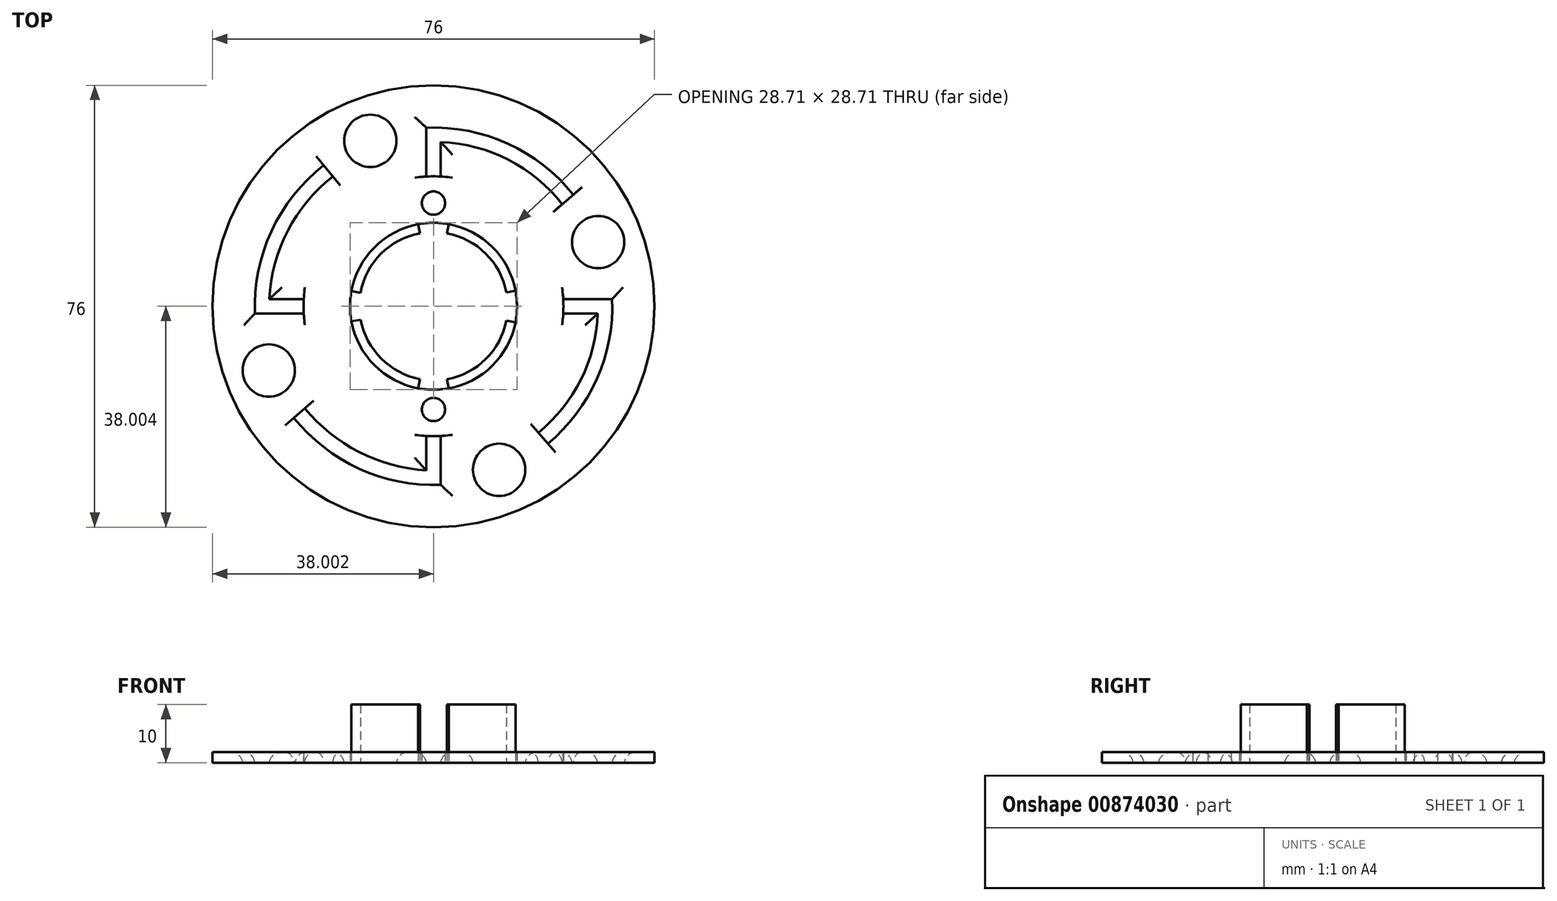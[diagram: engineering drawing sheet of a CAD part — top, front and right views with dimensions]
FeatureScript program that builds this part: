
annotation { "Feature Type Name" : "Feature", "Feature Type Description" : "" }
export const myFeature = defineFeature(function(context is Context, id is Id, definition is map)
    precondition{}
    {
        {
            var Q0;
            Q0=qCreatedBy(makeId("Top.planeOp"),FACE);
            var sketch = newSketch(context, id + "F0", { "sketchPlane" : qUnion([Q0])});
            skCircle(sketch, "E0", {"center": v(0, 0) * mm, "radius": 20.75 * mm});
            skCircle(sketch, "E1", {"center": v(0, 0) * mm, "radius": 22.35 * mm});
            skArc(sketch, "E2", {"start": v(-17.32, 22.32) * mm, "mid": v(-25.07, 12.97) * mm, "end": v(-28.22, 1.25) * mm});
            skLineSegment(sketch, "E3", {"start": v(-30.72, -1.25) * mm, "end": v(-20.71, -1.25) * mm});
            skLineSegment(sketch, "E4", {"start": v(-28.22, 1.25) * mm, "end": v(-20.71, 1.25) * mm});
            skArc(sketch, "E5", {"start": v(18.04, -21.74) * mm, "mid": v(25.36, -12.6) * mm, "end": v(28.22, -1.25) * mm});
            skLineSegment(sketch, "E6", {"start": v(30.72, 1.25) * mm, "end": v(20.71, 1.25) * mm});
            skLineSegment(sketch, "E7", {"start": v(28.22, -1.25) * mm, "end": v(20.71, -1.25) * mm});
            skArc(sketch, "E8", {"start": v(-22.14, -17.55) * mm, "mid": v(-12.8, -25.06) * mm, "end": v(-1.25, -28.22) * mm});
            skArc(sketch, "E9", {"start": v(22.14, 17.55) * mm, "mid": v(12.88, 25.2) * mm, "end": v(1.25, 28.22) * mm});
            skLineSegment(sketch, "E10", {"start": v(-1.25, -28.22) * mm, "end": v(-1.25, -20.71) * mm});
            skLineSegment(sketch, "E11", {"start": v(1.25, -20.71) * mm, "end": v(1.25, -30.72) * mm});
            skLineSegment(sketch, "E12", {"start": v(1.25, 28.22) * mm, "end": v(1.25, 20.71) * mm});
            skLineSegment(sketch, "E13", {"start": v(-1.25, 30.72) * mm, "end": v(-1.25, 20.71) * mm});
            skLineSegment(sketch, "E14", {"start": v(0, 20.75) * mm, "end": v(0, 17.75) * mm});
            skLineSegment(sketch, "E15", {"start": v(0, -20.75) * mm, "end": v(0, -17.75) * mm});
            skArc(sketch, "E16", {"start": v(-14.12, 2.6) * mm, "mid": v(-14.35, 0) * mm, "end": v(-14.12, -2.6) * mm});
            skArc(sketch, "E17", {"start": v(-2.61, -14.12) * mm, "mid": v(0, -14.35) * mm, "end": v(2.62, -14.12) * mm});
            skArc(sketch, "E18", {"start": v(14.1, -2.75) * mm, "mid": v(14.36, -0.03) * mm, "end": v(14.1, 2.7) * mm});
            skArc(sketch, "E19", {"start": v(2.61, 14.12) * mm, "mid": v(0, 14.36) * mm, "end": v(-2.61, 14.12) * mm});
            skCircle(sketch, "E20", {"center": v(11.28, -28.12) * mm, "radius": 4.5 * mm});
            skCircle(sketch, "E21", {"center": v(28.32, 11.04) * mm, "radius": 4.5 * mm});
            skCircle(sketch, "E22", {"center": v(-10.86, 28.46) * mm, "radius": 4.5 * mm});
            skCircle(sketch, "E23", {"center": v(-28.32, -11.04) * mm, "radius": 4.5 * mm});
            skLineSegment(sketch, "E24", {"start": v(-2.61, 14.12) * mm, "end": v(-2.32, 12.55) * mm});
            skLineSegment(sketch, "E25", {"start": v(2.61, 14.12) * mm, "end": v(2.32, 12.55) * mm});
            skLineSegment(sketch, "E26", {"start": v(-14.12, 2.6) * mm, "end": v(-12.55, 2.3) * mm});
            skLineSegment(sketch, "E27", {"start": v(-14.12, -2.6) * mm, "end": v(-12.55, -2.3) * mm});
            skLineSegment(sketch, "E28", {"start": v(-2.61, -14.12) * mm, "end": v(-2.32, -12.55) * mm});
            skLineSegment(sketch, "E29", {"start": v(14.1, 2.7) * mm, "end": v(12.53, 2.4) * mm});
            skLineSegment(sketch, "E30", {"start": v(14.1, -2.75) * mm, "end": v(12.52, -2.45) * mm});
            skLineSegment(sketch, "E31", {"start": v(2.62, -14.12) * mm, "end": v(2.32, -12.55) * mm});
            skArc(sketch, "E32", {"start": v(-12.55, -2.3) * mm, "mid": v(-8.99, -8.98) * mm, "end": v(-2.32, -12.55) * mm});
            skArc(sketch, "E33", {"start": v(-14.12, -2.6) * mm, "mid": v(-10.14, -10.13) * mm, "end": v(-2.61, -14.12) * mm});
            skArc(sketch, "E34", {"start": v(2.62, -14.12) * mm, "mid": v(10.12, -10.22) * mm, "end": v(14.1, -2.75) * mm});
            skArc(sketch, "E35", {"start": v(2.32, -12.55) * mm, "mid": v(8.99, -9.08) * mm, "end": v(12.52, -2.45) * mm});
            skArc(sketch, "E36", {"start": v(14.1, 2.7) * mm, "mid": v(10.13, 10.2) * mm, "end": v(2.61, 14.12) * mm});
            skArc(sketch, "E37", {"start": v(12.53, 2.4) * mm, "mid": v(9, 9.06) * mm, "end": v(2.32, 12.55) * mm});
            skArc(sketch, "E38", {"start": v(-2.32, 12.55) * mm, "mid": v(-9.04, 9.03) * mm, "end": v(-12.55, 2.3) * mm});
            skArc(sketch, "E39", {"start": v(-2.61, 14.12) * mm, "mid": v(-10.15, 10.15) * mm, "end": v(-14.12, 2.6) * mm});
            skPoint(sketch, "E40", {"position": v(-24.02, -19.2) * mm});
            skPoint(sketch, "E41", {"position": v(-18.9, 24.26) * mm});
            skPoint(sketch, "E42", {"position": v(24.02, 19.2) * mm});
            skPoint(sketch, "E43", {"position": v(19.68, -23.63) * mm});
            skArc(sketch, "E44", {"start": v(-24.02, -19.2) * mm, "mid": v(-12.75, -27.96) * mm, "end": v(1.25, -30.72) * mm});
            skArc(sketch, "E45", {"start": v(19.68, -23.63) * mm, "mid": v(28.11, -12.48) * mm, "end": v(30.72, 1.25) * mm});
            skArc(sketch, "E46", {"start": v(24.02, 19.2) * mm, "mid": v(12.77, 27.98) * mm, "end": v(-1.25, 30.72) * mm});
            skArc(sketch, "E47", {"start": v(-18.9, 24.26) * mm, "mid": v(-27.87, 12.92) * mm, "end": v(-30.72, -1.25) * mm});
            skLineSegment(sketch, "E48", {"start": v(-18.9, 24.26) * mm, "end": v(-17.32, 22.32) * mm});
            skLineSegment(sketch, "E49", {"start": v(22.14, 17.55) * mm, "end": v(24.02, 19.2) * mm});
            skLineSegment(sketch, "E50", {"start": v(18.04, -21.74) * mm, "end": v(19.68, -23.63) * mm});
            skLineSegment(sketch, "E51", {"start": v(-24.02, -19.2) * mm, "end": v(-22.14, -17.55) * mm});
            skCircle(sketch, "E52", {"center": v(0, 0) * mm, "radius": 38 * mm});
            skSolve(sketch);
        }
        {
            var Q0;
            Q0=makeQuery(id+"F0.imprint","IMPRINT",FACE,{"disambiguationData":[TD([[makeQuery(id+"F0.imprint","IMPRINT",EDGE,{"derivedFrom":sQuery(id+"F0.wireOp",EDGE,"JtYkX3aF-uqA7-pjmF-8fSk-2beL0rNtP7QC")}),-1.0]])]});
            var Q1;
            Q1=makeQuery(id+"F0.imprint","IMPRINT",FACE,{"disambiguationData":[TD([[makeQuery(id+"F0.imprint","IMPRINT",EDGE,{"derivedFrom":sQuery(id+"F0.wireOp",EDGE,"8JJW8lRD-QEWP-9C01-VRjb-YcTUdrWMRwsa")}),1.0]])]});
            var Q2;
            {var subQ1=sQuery(id+"F0.wireOp",EDGE,"NE2U6Hh3-jpx8-j1Jv-iiVe-F0KoeOMKkSiu");Q2=makeQuery(id+"F0.imprint","IMPRINT",FACE,{"disambiguationData":[TD([[makeQuery(id+"F0.imprint","IMPRINT",EDGE,{"derivedFrom":subQ1}),-1.0]])]});}
            var Q3;
            {var subQ1=sQuery(id+"F0.wireOp",EDGE,"E5");Q3=makeQuery(id+"F0.imprint","IMPRINT",FACE,{"disambiguationData":[TD([[makeQuery(id+"F0.imprint","IMPRINT",EDGE,{"derivedFrom":subQ1}),1.0]])]});}
            var Q4;
            {var subQ0=sQuery(id+"F0.wireOp",EDGE,"E4");var subQ1=sQuery(id+"F0.wireOp",EDGE,"E0");var subQ2=makeQuery(id+"F0.imprint","INTERSECT",VERTEX,{"derivedFrom":[subQ1,subQ0]});Q4=makeQuery(id+"F0.imprint","IMPRINT",FACE,{"disambiguationData":[TD([[makeQuery(id+"F0.imprint","IMPRINT",EDGE,{"disambiguationData":[TD([[subQ2,1.0]])],"derivedFrom":subQ1}),-1.0]])]});}
            var Q5;
            {var subQ0=sQuery(id+"F0.wireOp",EDGE,"E3");var subQ1=sQuery(id+"F0.wireOp",EDGE,"E0");var subQ2=makeQuery(id+"F0.imprint","INTERSECT",VERTEX,{"derivedFrom":[subQ1,subQ0]});Q5=makeQuery(id+"F0.imprint","IMPRINT",FACE,{"disambiguationData":[TD([[makeQuery(id+"F0.imprint","IMPRINT",EDGE,{"disambiguationData":[TD([[subQ2,1.0]])],"derivedFrom":subQ1}),-1.0]])]});}
            var Q6;
            {var subQ0=sQuery(id+"F0.wireOp",EDGE,"E10");var subQ1=sQuery(id+"F0.wireOp",EDGE,"E0");var subQ2=makeQuery(id+"F0.imprint","INTERSECT",VERTEX,{"derivedFrom":[subQ1,subQ0]});Q6=makeQuery(id+"F0.imprint","IMPRINT",FACE,{"disambiguationData":[TD([[makeQuery(id+"F0.imprint","IMPRINT",EDGE,{"disambiguationData":[TD([[subQ2,-1.0]])],"derivedFrom":subQ1}),-1.0]])]});}
            var Q7;
            {var subQ0=sQuery(id+"F0.wireOp",EDGE,"E7");var subQ1=sQuery(id+"F0.wireOp",EDGE,"E0");var subQ2=makeQuery(id+"F0.imprint","INTERSECT",VERTEX,{"derivedFrom":[subQ1,subQ0]});Q7=makeQuery(id+"F0.imprint","IMPRINT",FACE,{"disambiguationData":[TD([[makeQuery(id+"F0.imprint","IMPRINT",EDGE,{"disambiguationData":[TD([[subQ2,1.0]])],"derivedFrom":subQ1}),-1.0]])]});}
            var Q8;
            {var subQ0=sQuery(id+"F0.wireOp",EDGE,"E6");var subQ1=sQuery(id+"F0.wireOp",EDGE,"E0");var subQ2=makeQuery(id+"F0.imprint","INTERSECT",VERTEX,{"derivedFrom":[subQ1,subQ0]});Q8=makeQuery(id+"F0.imprint","IMPRINT",FACE,{"disambiguationData":[TD([[makeQuery(id+"F0.imprint","IMPRINT",EDGE,{"disambiguationData":[TD([[subQ2,1.0]])],"derivedFrom":subQ1}),-1.0]])]});}
            var Q9;
            {var subQ0=sQuery(id+"F0.wireOp",EDGE,"E6");var subQ1=sQuery(id+"F0.wireOp",EDGE,"E0");var subQ2=makeQuery(id+"F0.imprint","INTERSECT",VERTEX,{"derivedFrom":[subQ1,subQ0]});Q9=makeQuery(id+"F0.imprint","IMPRINT",FACE,{"disambiguationData":[TD([[makeQuery(id+"F0.imprint","IMPRINT",EDGE,{"disambiguationData":[TD([[subQ2,-1.0]])],"derivedFrom":subQ1}),-1.0]])]});}
            var Q10;
            {var subQ0=sQuery(id+"F0.wireOp",EDGE,"E12");var subQ1=sQuery(id+"F0.wireOp",EDGE,"E0");var subQ2=makeQuery(id+"F0.imprint","INTERSECT",VERTEX,{"derivedFrom":[subQ1,subQ0]});Q10=makeQuery(id+"F0.imprint","IMPRINT",FACE,{"disambiguationData":[TD([[makeQuery(id+"F0.imprint","IMPRINT",EDGE,{"disambiguationData":[TD([[subQ2,-1.0]])],"derivedFrom":subQ1}),-1.0]])]});}
            var Q11;
            {var subQ0=sQuery(id+"F0.wireOp",EDGE,"E3");var subQ1=sQuery(id+"F0.wireOp",EDGE,"E0");var subQ2=makeQuery(id+"F0.imprint","INTERSECT",VERTEX,{"derivedFrom":[subQ1,subQ0]});Q11=makeQuery(id+"F0.imprint","IMPRINT",FACE,{"disambiguationData":[TD([[makeQuery(id+"F0.imprint","IMPRINT",EDGE,{"disambiguationData":[TD([[subQ2,-1.0]])],"derivedFrom":subQ1}),-1.0]])]});}
            var Q12;
            {var subQ0=sQuery(id+"F0.wireOp",EDGE,"E0");var subQ5=makeQuery(id+"F0.imprint","INTERSECT",VERTEX,{"derivedFrom":[subQ0,sQuery(id+"F0.wireOp",EDGE,"E6")]});Q12=makeQuery(id+"F0.imprint","IMPRINT",FACE,{"disambiguationData":[TD([[makeQuery(id+"F0.imprint","IMPRINT",EDGE,{"disambiguationData":[TD([[subQ5,-1.0]])],"derivedFrom":subQ0}),1.0]])]});}
            var Q13;
            Q13=makeQuery(id+"F0.imprint","IMPRINT",FACE,{"disambiguationData":[TD([[makeQuery(id+"F0.imprint","IMPRINT",EDGE,{"derivedFrom":sQuery(id+"F0.wireOp",EDGE,"3ZusnNTy-GkZT-iUSi-foyf-aXQAiV7al5yb")}),-1.0]])]});
            extrude(context, id + "F1", {"entities" : qUnion([Q0, Q1, Q2, Q3, Q4, Q5, Q6, Q7, Q8, Q9, Q10, Q11, Q12, Q13]), "depth" : 1.8 * mm, "offsetDistance" : 25 * mm});
        }
        {
            var Q0;
            Q0=sQuery(id+"F0.wireOp",VERTEX,"E15.end");
            var Q1;
            Q1=sQuery(id+"F0.wireOp",VERTEX,"E14.end");
            var Q2;
            Q2=makeQuery(id+"F1.opExtrude","SWEPT_BODY",BODY,{"disambiguationData":[OSD([sQuery(id+"F0.wireOp",EDGE,"E1"),sQuery(id+"F0.wireOp",EDGE,"JtYkX3aF-uqA7-pjmF-8fSk-2beL0rNtP7QC"),sQuery(id+"F0.wireOp",EDGE,"8JJW8lRD-QEWP-9C01-VRjb-YcTUdrWMRwsa"),sQuery(id+"F0.wireOp",EDGE,"uFhvHYX3-8JKD-H8n8-qWPz-aUgkWJzXKccN"),sQuery(id+"F0.wireOp",EDGE,"E2"),sQuery(id+"F0.wireOp",EDGE,"E3"),sQuery(id+"F0.wireOp",EDGE,"E4"),sQuery(id+"F0.wireOp",EDGE,"E5"),sQuery(id+"F0.wireOp",EDGE,"NE2U6Hh3-jpx8-j1Jv-iiVe-F0KoeOMKkSiu"),sQuery(id+"F0.wireOp",EDGE,"E6"),sQuery(id+"F0.wireOp",EDGE,"E7"),sQuery(id+"F0.wireOp",EDGE,"ZG8jGtW0-kf8V-TbsZ-LPp7-RuGRRNqqyVkH"),sQuery(id+"F0.wireOp",EDGE,"fmeD1r8i-8Wsa-lR9i-GNXP-AYA1yHY84zb3"),sQuery(id+"F0.wireOp",EDGE,"bjy13ZNf-o2fh-lKbF-fSuF-RSpPyinbBZMj"),sQuery(id+"F0.wireOp",EDGE,"E8"),sQuery(id+"F0.wireOp",EDGE,"YXEZxhNc-pCvv-fJSu-8syy-bRr3xrhN3yT2"),sQuery(id+"F0.wireOp",EDGE,"nJSUC5IB-OxOl-JQJy-F9vk-B84e3hYhLg1p"),sQuery(id+"F0.wireOp",EDGE,"E9"),sQuery(id+"F0.wireOp",EDGE,"A251WNtt-zrTg-3Hvl-hV5r-WAsRRatjA8sI"),sQuery(id+"F0.wireOp",EDGE,"ZfxGHPmq-kaDy-ZfHD-nUsA-2Ftj0pm5jEMy"),sQuery(id+"F0.wireOp",EDGE,"E10"),sQuery(id+"F0.wireOp",EDGE,"E11"),sQuery(id+"F0.wireOp",EDGE,"E12"),sQuery(id+"F0.wireOp",EDGE,"E13"),sQuery(id+"F0.wireOp",EDGE,"weULgePI-roOJ-cMUK-peC7-qsmyXOXqrT9m"),sQuery(id+"F0.wireOp",EDGE,"UDUuayih-Ka7P-NoIc-IkLO-qXrikWTbf6pt"),sQuery(id+"F0.wireOp",EDGE,"T07nDOxv-luDJ-uSm4-Lqdw-o2tEsc6Tqr3Y"),sQuery(id+"F0.wireOp",EDGE,"01p4Yr1x-TUeZ-ZZvR-0jQk-AZIFxx44rd4s"),sQuery(id+"F0.wireOp",EDGE,"mddWgEqq-aVu1-2llw-zfOM-TSO3SZ2z48u3")])]});
            hole(context, id + "F2", {"style" : HoleStyle.SIMPLE, "endStyle" : HoleEndStyle.THROUGH, "oppositeDirection" : true, "holeDiameter" : 4 * mm, "majorDiameter" : 5 * mm, "isTappedThrough" : true, "tappedDepth" : 12 * mm, "tapClearance" : 3, "locations" : qUnion([Q0, Q1]), "scope" : qUnion([Q2])});
        }
        {
            var Q0;
            Q0=makeQuery(id+"F1.opExtrude","CAP_EDGE",EDGE,{"disambiguationData":[OSD([sQuery(id+"F0.wireOp",EDGE,"mddWgEqq-aVu1-2llw-zfOM-TSO3SZ2z48u3")])],"isStart":false});
            var Q1;
            Q1=makeQuery(id+"F1.opExtrude","CAP_EDGE",EDGE,{"disambiguationData":[OSD([sQuery(id+"F0.wireOp",EDGE,"UDUuayih-Ka7P-NoIc-IkLO-qXrikWTbf6pt")])],"isStart":false});
            var Q2;
            Q2=makeQuery(id+"F1.opExtrude","CAP_EDGE",EDGE,{"disambiguationData":[OSD([sQuery(id+"F0.wireOp",EDGE,"01p4Yr1x-TUeZ-ZZvR-0jQk-AZIFxx44rd4s")])],"isStart":false});
            var Q3;
            Q3=makeQuery(id+"F1.opExtrude","CAP_EDGE",EDGE,{"disambiguationData":[OSD([sQuery(id+"F0.wireOp",EDGE,"T07nDOxv-luDJ-uSm4-Lqdw-o2tEsc6Tqr3Y")])],"isStart":false});
            var Q4;
            Q4=makeQuery(id+"F1.opExtrude","CAP_EDGE",EDGE,{"disambiguationData":[OSD([sQuery(id+"F0.wireOp",EDGE,"E5")])],"isStart":false});
            var Q5;
            Q5=makeQuery(id+"F1.opExtrude","CAP_EDGE",EDGE,{"disambiguationData":[OSD([sQuery(id+"F0.wireOp",EDGE,"E8")])],"isStart":false});
            var Q6;
            Q6=makeQuery(id+"F1.opExtrude","CAP_EDGE",EDGE,{"disambiguationData":[OSD([sQuery(id+"F0.wireOp",EDGE,"E2")])],"isStart":false});
            var Q7;
            Q7=makeQuery(id+"F1.opExtrude","CAP_EDGE",EDGE,{"disambiguationData":[OSD([sQuery(id+"F0.wireOp",EDGE,"E9")])],"isStart":false});
            var Q8;
            Q8=makeQuery(id+"F1.opExtrude","CAP_EDGE",EDGE,{"disambiguationData":[OSD([sQuery(id+"F0.wireOp",EDGE,"8JJW8lRD-QEWP-9C01-VRjb-YcTUdrWMRwsa")])],"isStart":false});
            var Q9;
            Q9=makeQuery(id+"F1.opExtrude","CAP_EDGE",EDGE,{"disambiguationData":[OSD([sQuery(id+"F0.wireOp",EDGE,"JtYkX3aF-uqA7-pjmF-8fSk-2beL0rNtP7QC")])],"isStart":false});
            var Q10;
            Q10=makeQuery(id+"F1.opExtrude","CAP_EDGE",EDGE,{"disambiguationData":[OSD([sQuery(id+"F0.wireOp",EDGE,"E4")])],"isStart":false});
            var Q11;
            Q11=makeQuery(id+"F1.opExtrude","CAP_EDGE",EDGE,{"disambiguationData":[OSD([sQuery(id+"F0.wireOp",EDGE,"E3")])],"isStart":false});
            var Q12;
            Q12=makeQuery(id+"F1.opExtrude","CAP_EDGE",EDGE,{"disambiguationData":[OSD([sQuery(id+"F0.wireOp",EDGE,"E13")])],"isStart":false});
            var Q13;
            Q13=makeQuery(id+"F1.opExtrude","CAP_EDGE",EDGE,{"disambiguationData":[OSD([sQuery(id+"F0.wireOp",EDGE,"E12")])],"isStart":false});
            var Q14;
            Q14=makeQuery(id+"F1.opExtrude","CAP_EDGE",EDGE,{"disambiguationData":[OSD([sQuery(id+"F0.wireOp",EDGE,"E6")])],"isStart":false});
            var Q15;
            Q15=makeQuery(id+"F1.opExtrude","CAP_EDGE",EDGE,{"disambiguationData":[OSD([sQuery(id+"F0.wireOp",EDGE,"E7")])],"isStart":false});
            var Q16;
            Q16=makeQuery(id+"F1.opExtrude","CAP_EDGE",EDGE,{"disambiguationData":[OSD([sQuery(id+"F0.wireOp",EDGE,"nJSUC5IB-OxOl-JQJy-F9vk-B84e3hYhLg1p")])],"isStart":false});
            var Q17;
            Q17=makeQuery(id+"F1.opExtrude","CAP_EDGE",EDGE,{"disambiguationData":[OSD([sQuery(id+"F0.wireOp",EDGE,"ZfxGHPmq-kaDy-ZfHD-nUsA-2Ftj0pm5jEMy")])],"isStart":false});
            var Q18;
            Q18=makeQuery(id+"F1.opExtrude","CAP_EDGE",EDGE,{"disambiguationData":[OSD([sQuery(id+"F0.wireOp",EDGE,"A251WNtt-zrTg-3Hvl-hV5r-WAsRRatjA8sI")])],"isStart":false});
            var Q19;
            Q19=makeQuery(id+"F1.opExtrude","CAP_EDGE",EDGE,{"disambiguationData":[OSD([sQuery(id+"F0.wireOp",EDGE,"weULgePI-roOJ-cMUK-peC7-qsmyXOXqrT9m")])],"isStart":false});
            var Q20;
            Q20=makeQuery(id+"F1.opExtrude","CAP_EDGE",EDGE,{"disambiguationData":[OSD([sQuery(id+"F0.wireOp",EDGE,"YXEZxhNc-pCvv-fJSu-8syy-bRr3xrhN3yT2")])],"isStart":false});
            var Q21;
            Q21=makeQuery(id+"F1.opExtrude","CAP_EDGE",EDGE,{"disambiguationData":[OSD([sQuery(id+"F0.wireOp",EDGE,"E10")])],"isStart":false});
            var Q22;
            Q22=makeQuery(id+"F1.opExtrude","CAP_EDGE",EDGE,{"disambiguationData":[OSD([sQuery(id+"F0.wireOp",EDGE,"E11")])],"isStart":false});
            var Q23;
            Q23=makeQuery(id+"F1.opExtrude","CAP_EDGE",EDGE,{"disambiguationData":[OSD([sQuery(id+"F0.wireOp",EDGE,"ZG8jGtW0-kf8V-TbsZ-LPp7-RuGRRNqqyVkH")])],"isStart":false});
            var Q24;
            Q24=makeQuery(id+"F1.opExtrude","CAP_EDGE",EDGE,{"disambiguationData":[OSD([sQuery(id+"F0.wireOp",EDGE,"fmeD1r8i-8Wsa-lR9i-GNXP-AYA1yHY84zb3")])],"isStart":false});
            var Q25;
            Q25=makeQuery(id+"F1.opExtrude","CAP_EDGE",EDGE,{"disambiguationData":[OSD([sQuery(id+"F0.wireOp",EDGE,"bjy13ZNf-o2fh-lKbF-fSuF-RSpPyinbBZMj")])],"isStart":false});
            var Q26;
            Q26=makeQuery(id+"F1.opExtrude","CAP_EDGE",EDGE,{"disambiguationData":[OSD([sQuery(id+"F0.wireOp",EDGE,"NE2U6Hh3-jpx8-j1Jv-iiVe-F0KoeOMKkSiu")])],"isStart":false});
            var Q27;
            Q27=makeQuery(id+"F1.opExtrude","CAP_EDGE",EDGE,{"disambiguationData":[OSD([sQuery(id+"F0.wireOp",EDGE,"E47")])],"isStart":false});
            var Q28;
            Q28=makeQuery(id+"F1.opExtrude","CAP_EDGE",EDGE,{"disambiguationData":[OSD([sQuery(id+"F0.wireOp",EDGE,"E23")])],"isStart":false});
            var Q29;
            Q29=makeQuery(id+"F1.opExtrude","CAP_EDGE",EDGE,{"disambiguationData":[OSD([sQuery(id+"F0.wireOp",EDGE,"E22")])],"isStart":false});
            var Q30;
            Q30=makeQuery(id+"F1.opExtrude","CAP_EDGE",EDGE,{"disambiguationData":[OSD([sQuery(id+"F0.wireOp",EDGE,"E44")])],"isStart":false});
            var Q31;
            Q31=makeQuery(id+"F1.opExtrude","CAP_EDGE",EDGE,{"disambiguationData":[OSD([sQuery(id+"F0.wireOp",EDGE,"E45")])],"isStart":false});
            var Q32;
            Q32=makeQuery(id+"F1.opExtrude","CAP_EDGE",EDGE,{"disambiguationData":[OSD([sQuery(id+"F0.wireOp",EDGE,"E46")])],"isStart":false});
            var Q33;
            Q33=makeQuery(id+"F1.opExtrude","CAP_EDGE",EDGE,{"disambiguationData":[OSD([sQuery(id+"F0.wireOp",EDGE,"E21")])],"isStart":false});
            var Q34;
            Q34=makeQuery(id+"F1.opExtrude","CAP_EDGE",EDGE,{"disambiguationData":[OSD([sQuery(id+"F0.wireOp",EDGE,"E20")])],"isStart":false});
            fillet(context, id + "F3", {"entities" : qUnion([Q0, Q1, Q2, Q3, Q4, Q5, Q6, Q7, Q8, Q9, Q10, Q11, Q12, Q13, Q14, Q15, Q16, Q17, Q18, Q19, Q20, Q21, Q22, Q23, Q24, Q25, Q26, Q27, Q28, Q29, Q30, Q31, Q32, Q33, Q34]), "radius" : 2 * mm, "tangentPropagation" : true, "allowEdgeOverflow" : false});
        }
        {
            var Q0;
            Q0=makeQuery(id+"F0.imprint","IMPRINT",FACE,{"disambiguationData":[TD([[makeQuery(id+"F0.imprint","IMPRINT",EDGE,{"derivedFrom":sQuery(id+"F0.wireOp",EDGE,"E24")}),-1.0]])]});
            var Q1;
            Q1=makeQuery(id+"F0.imprint","IMPRINT",FACE,{"disambiguationData":[TD([[makeQuery(id+"F0.imprint","IMPRINT",EDGE,{"derivedFrom":sQuery(id+"F0.wireOp",EDGE,"E27")}),-1.0]])]});
            var Q2;
            Q2=makeQuery(id+"F0.imprint","IMPRINT",FACE,{"disambiguationData":[TD([[makeQuery(id+"F0.imprint","IMPRINT",EDGE,{"derivedFrom":sQuery(id+"F0.wireOp",EDGE,"E30")}),1.0]])]});
            var Q3;
            Q3=makeQuery(id+"F0.imprint","IMPRINT",FACE,{"disambiguationData":[TD([[makeQuery(id+"F0.imprint","IMPRINT",EDGE,{"derivedFrom":sQuery(id+"F0.wireOp",EDGE,"E25")}),1.0]])]});
            extrude(context, id + "F4", {"entities" : qUnion([Q0, Q1, Q2, Q3]), "operationType" : NewBodyOperationType.ADD, "depth" : 10 * mm, "offsetDistance" : 25 * mm});
        }
    });
